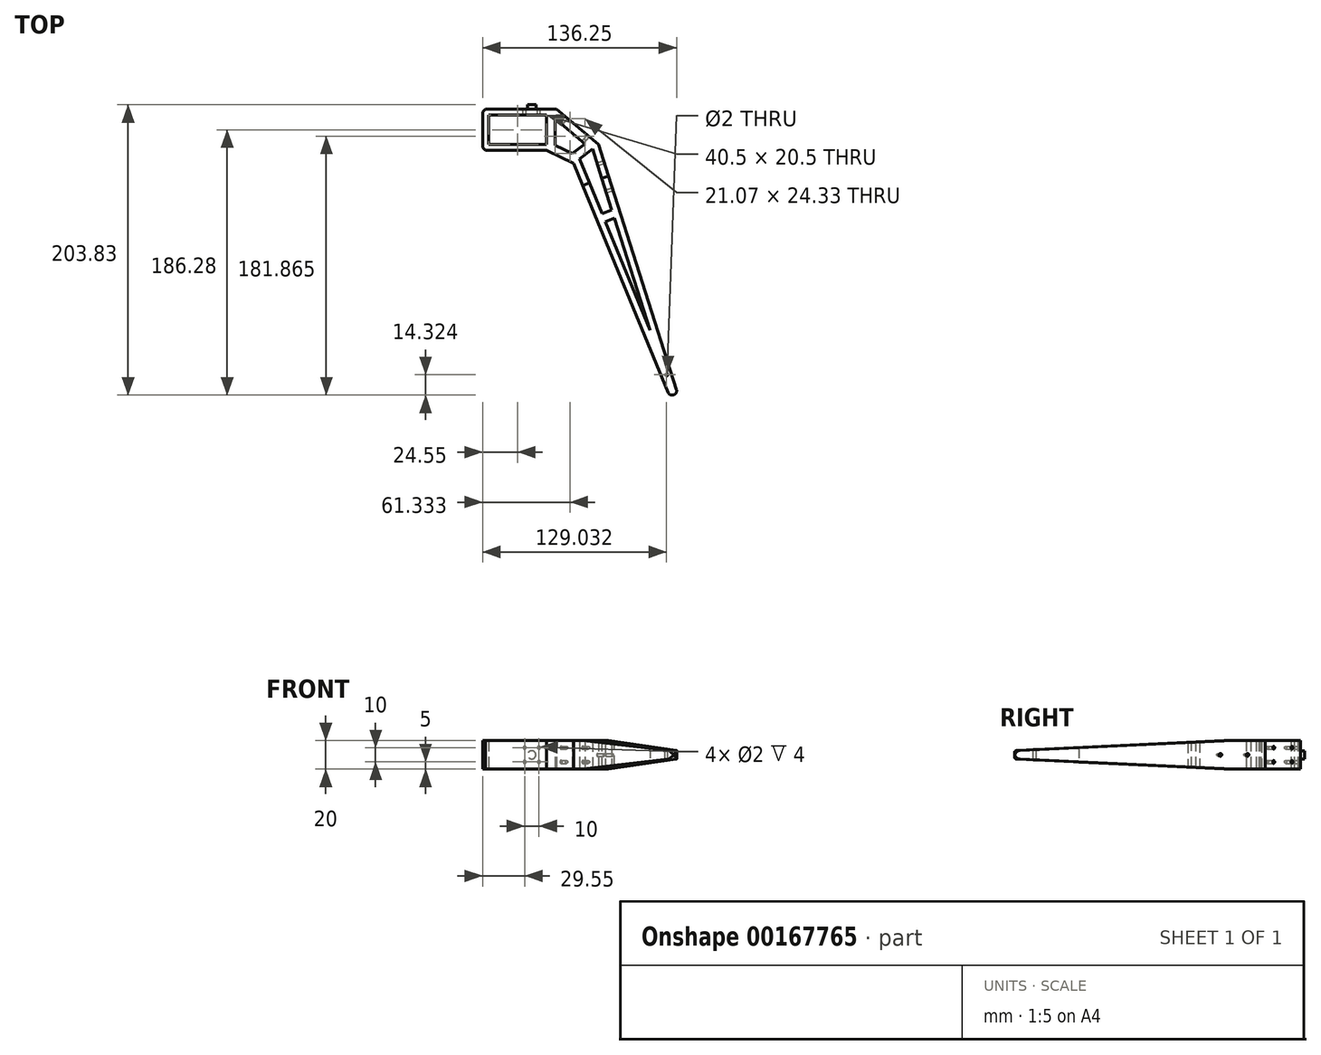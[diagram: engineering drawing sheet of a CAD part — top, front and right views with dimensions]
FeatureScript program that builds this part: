
annotation { "Feature Type Name" : "Feature", "Feature Type Description" : "" }
export const myFeature = defineFeature(function(context is Context, id is Id, definition is map)
    precondition{}
    {
        {
            var Q0;
            Q0=qCreatedBy(makeId("Top.planeOp"),FACE);
            var sketch = newSketch(context, id + "F0", { "sketchPlane" : qUnion([Q0])});
            skLineSegment(sketch, "E0.bottom", {"start": v(-40.5, 20.5) * mm, "end": v(0, 20.5) * mm});
            skLineSegment(sketch, "E0.top", {"start": v(-40.5, 0) * mm, "end": v(0, 0) * mm});
            skLineSegment(sketch, "E0.left", {"start": v(-40.5, 20.5) * mm, "end": v(-40.5, 0) * mm});
            skLineSegment(sketch, "E0.right", {"start": v(0, 20.5) * mm, "end": v(0, 0) * mm});
            skLineSegment(sketch, "E1", {"start": v(-44.8, 24.8) * mm, "end": v(-44.8, -4.3) * mm});
            skLineSegment(sketch, "E2", {"start": v(-44.8, -4.3) * mm, "end": v(0, -4.3) * mm});
            skLineSegment(sketch, "E3", {"start": v(0, -4.3) * mm, "end": v(19.04, -13.31) * mm});
            skLineSegment(sketch, "E4", {"start": v(36.56, 0) * mm, "end": v(7, 24.8) * mm});
            skLineSegment(sketch, "E5", {"start": v(7, 24.8) * mm, "end": v(-44.8, 24.8) * mm});
            skLineSegment(sketch, "E6", {"start": v(0, 20.5) * mm, "end": v(0, 24.8) * mm, "construction": true});
            skLineSegment(sketch, "E7", {"start": v(-40.5, 0) * mm, "end": v(-44.8, 0) * mm, "construction": true});
            skLineSegment(sketch, "E8", {"start": v(0, 0) * mm, "end": v(0, -4.3) * mm, "construction": true});
            skLineSegment(sketch, "E9", {"start": v(6, 18) * mm, "end": v(6, -0.5) * mm});
            skLineSegment(sketch, "E10", {"start": v(6, -0.5) * mm, "end": v(18.31, -6.33) * mm});
            skLineSegment(sketch, "E11", {"start": v(18.31, -6.33) * mm, "end": v(27.07, 0.32) * mm});
            skLineSegment(sketch, "E12", {"start": v(27.07, 0.32) * mm, "end": v(6, 18) * mm});
            skLineSegment(sketch, "E13", {"start": v(0, 10.25) * mm, "end": v(6, 10.25) * mm, "construction": true});
            skLineSegment(sketch, "E14", {"start": v(27.07, 0.32) * mm, "end": v(31.84, 3.95) * mm, "construction": true});
            skLineSegment(sketch, "E15", {"start": v(6, -0.5) * mm, "end": v(3.43, -5.93) * mm, "construction": true});
            skLineSegment(sketch, "E16", {"start": v(-40.5, 0) * mm, "end": v(0, 20.5) * mm, "construction": true});
            skLineSegment(sketch, "E17", {"start": v(-20.25, 10.25) * mm, "end": v(0, 0) * mm, "construction": true});
            skLineSegment(sketch, "E18", {"start": v(30.7, -4.45) * mm, "end": v(27.07, 0.32) * mm, "construction": true});
            skLineSegment(sketch, "E19", {"start": v(25.76, 60.45) * mm, "end": v(30.7, 61.23) * mm, "construction": true});
            skLineSegment(sketch, "E20", {"start": v(19.04, -13.31) * mm, "end": v(36.56, 0) * mm, "construction": true});
            skLineSegment(sketch, "E21", {"start": v(27.8, -6.66) * mm, "end": v(89.36, -175.8) * mm, "construction": true});
            skLineSegment(sketch, "E22", {"start": v(36.56, 0) * mm, "end": v(92.18, -174.78) * mm});
            skLineSegment(sketch, "E23", {"start": v(92.18, -174.78) * mm, "end": v(86.54, -176.83) * mm});
            skLineSegment(sketch, "E24", {"start": v(86.54, -176.83) * mm, "end": v(19.04, -13.31) * mm});
            skLineSegment(sketch, "E25", {"start": v(32.33, -3.21) * mm, "end": v(23.16, -10.18) * mm});
            skLineSegment(sketch, "E26", {"start": v(23.16, -10.18) * mm, "end": v(72.9, -130.66) * mm});
            skLineSegment(sketch, "E27", {"start": v(72.9, -130.66) * mm, "end": v(32.33, -3.21) * mm});
            skLineSegment(sketch, "E28", {"start": v(72.9, -130.66) * mm, "end": v(77.66, -129.14) * mm, "construction": true});
            skLineSegment(sketch, "E29", {"start": v(72.9, -130.66) * mm, "end": v(68.27, -132.57) * mm, "construction": true});
            skLineSegment(sketch, "E30", {"start": v(-30.5, 10.25) * mm, "end": v(89.36, -175.8) * mm, "construction": true});
            skLineSegment(sketch, "E31", {"start": v(-40.5, 10.25) * mm, "end": v(-30.5, 10.25) * mm, "construction": true});
            skSolve(sketch);
        }
        {
            var Q0;
            Q0=makeQuery(id+"F0.imprint","IMPRINT",FACE,{"disambiguationData":[TD([[makeQuery(id+"F0.imprint","IMPRINT",EDGE,{"derivedFrom":sQuery(id+"F0.wireOp",EDGE,"E0.bottom")}),1.0]])]});
            extrude(context, id + "F1", {"entities" : qUnion([Q0]), "endBound" : BoundingType.SYMMETRIC, "depth" : 20 * mm});
        }
        {
            var Q0;
            Q0=makeQuery(id+"F1.opExtrude","SWEPT_EDGE",EDGE,{"disambiguationData":[OSD([sQuery(id+"F0.wireOp",EDGE,"E1"),sQuery(id+"F0.wireOp",EDGE,"E5")])]});
            var Q1;
            Q1=makeQuery(id+"F1.opExtrude","SWEPT_EDGE",EDGE,{"disambiguationData":[OSD([sQuery(id+"F0.wireOp",EDGE,"E1"),sQuery(id+"F0.wireOp",EDGE,"E2")])]});
            chamfer(context, id + "F2", {"entities" : qUnion([Q0, Q1]), "width" : 2 * mm, "tangentPropagation" : true});
        }
        {
            var Q0;
            Q0=makeQuery(id+"F1.opExtrude","SWEPT_FACE",FACE,{"disambiguationData":[OSD([sQuery(id+"F0.wireOp",EDGE,"E5")])]});
            var sketch = newSketch(context, id + "F3", { "sketchPlane" : qUnion([Q0])});
            skLineSegment(sketch, "E32", {"start": v(10.25, 42.18) * mm, "end": v(10.25, -42.18) * mm, "construction": true});
            skCircle(sketch, "E33", {"center": v(10.25, 0) * mm, "radius": 2.9 * mm});
            skSolve(sketch);
        }
        {
            var Q0;
            Q0 = qSketchRegion(id + "F3", true);
            extrude(context, id + "F4", {"entities" : qUnion([Q0]), "operationType" : NewBodyOperationType.ADD, "depth" : 3 * mm});
        }
        {
            var Q0;
            Q0=makeQuery(id+"F1.opExtrude","CAP_VERTEX",VERTEX,{"disambiguationData":[OSD([sQuery(id+"F0.wireOp",EDGE,"E23"),sQuery(id+"F0.wireOp",EDGE,"E24")])],"isStart":true});
            var Q1;
            Q1=makeQuery(id+"F1.opExtrude","CAP_VERTEX",VERTEX,{"disambiguationData":[OSD([sQuery(id+"F0.wireOp",EDGE,"E22"),sQuery(id+"F0.wireOp",EDGE,"E23")])],"isStart":true});
            cPlane(context, id + "F5", {"entities" : qUnion([Q0, Q1]), "cplaneType" : CPlaneType.MID_PLANE, "offset" : 25 * mm, "width" : 150 * mm, "height" : 150 * mm});
        }
        {
            var Q0;
            Q0=qCreatedBy(id+"F5.planeOp",FACE);
            var sketch = newSketch(context, id + "F6", { "sketchPlane" : qUnion([Q0])});
            skLineSegment(sketch, "E34", {"start": v(-195.76, -3) * mm, "end": v(-35.76, -10) * mm});
            skLineSegment(sketch, "E35", {"start": v(-35.76, -10) * mm, "end": v(-195.76, -10) * mm});
            skLineSegment(sketch, "E36", {"start": v(-195.76, -10) * mm, "end": v(-195.76, -3) * mm});
            skLineSegment(sketch, "E37.MirrorCS", {"start": v(-195.76, 10) * mm, "end": v(-195.76, 3) * mm});
            skLineSegment(sketch, "E38.MirrorCS", {"start": v(-195.76, 3) * mm, "end": v(-35.76, 10) * mm});
            skLineSegment(sketch, "E39.MirrorCS", {"start": v(-35.76, 10) * mm, "end": v(-195.76, 10) * mm});
            skSolve(sketch);
        }
        {
            var Q0;
            Q0 = qSketchRegion(id + "F6", true);
            extrude(context, id + "F7", {"entities" : qUnion([Q0]), "operationType" : NewBodyOperationType.REMOVE, "endBound" : BoundingType.THROUGH_ALL, "oppositeDirection" : true, "depth" : 25 * mm, "hasSecondDirection" : true, "secondDirectionBound" : SecondDirectionBoundingType.THROUGH_ALL, "secondDirectionOppositeDirection" : false, "secondDirectionDepth" : 25 * mm});
        }
        {
            var Q0;
            Q0=makeQuery(id+"F1.opExtrude","SWEPT_EDGE",EDGE,{"disambiguationData":[OSD([sQuery(id+"F0.wireOp",EDGE,"E22"),sQuery(id+"F0.wireOp",EDGE,"E23")])]});
            var Q1;
            Q1=makeQuery(id+"F7.boolean.opBoolean","COPY",EDGE,{"derivedFrom":makeQuery(id+"F7.opExtrude","SWEPT_EDGE",EDGE,{"disambiguationData":[OSD([sQuery(id+"F6.wireOp",EDGE,"E37.MirrorCS"),sQuery(id+"F6.wireOp",EDGE,"E38.MirrorCS")])]})});
            var Q2;
            Q2=makeQuery(id+"F1.opExtrude","SWEPT_EDGE",EDGE,{"disambiguationData":[OSD([sQuery(id+"F0.wireOp",EDGE,"E23"),sQuery(id+"F0.wireOp",EDGE,"E24")])]});
            var Q3;
            Q3=makeQuery(id+"F7.boolean.opBoolean","COPY",EDGE,{"derivedFrom":makeQuery(id+"F7.opExtrude","SWEPT_EDGE",EDGE,{"disambiguationData":[OSD([sQuery(id+"F6.wireOp",EDGE,"E34"),sQuery(id+"F6.wireOp",EDGE,"E36")])]})});
            fillet(context, id + "F8", {"entities" : qUnion([Q0, Q1, Q2, Q3]), "radius" : 3 * mm, "tangentPropagation" : true});
        }
        {
            var Q0;
            Q0=makeQuery(id+"F1.opExtrude","SWEPT_FACE",FACE,{"disambiguationData":[OSD([sQuery(id+"F0.wireOp",EDGE,"E5")])]});
            var sketch = newSketch(context, id + "F9", { "sketchPlane" : qUnion([Q0])});
            skLineSegment(sketch, "E40.bottom", {"start": v(15.25, 5) * mm, "end": v(5.25, 5) * mm, "construction": true});
            skLineSegment(sketch, "E40.top", {"start": v(15.25, -5) * mm, "end": v(5.25, -5) * mm, "construction": true});
            skLineSegment(sketch, "E40.left", {"start": v(15.25, 5) * mm, "end": v(15.25, -5) * mm, "construction": true});
            skLineSegment(sketch, "E40.right", {"start": v(5.25, 5) * mm, "end": v(5.25, -5) * mm, "construction": true});
            skLineSegment(sketch, "E41", {"start": v(15.25, 5) * mm, "end": v(5.25, -5) * mm, "construction": true});
            skLineSegment(sketch, "E42", {"start": v(10.25, 0) * mm, "end": v(15.25, -5) * mm, "construction": true});
            skCircle(sketch, "E43", {"center": v(15.25, 5) * mm, "radius": 1 * mm});
            skCircle(sketch, "E44", {"center": v(15.25, -5) * mm, "radius": 1 * mm});
            skCircle(sketch, "E45", {"center": v(5.25, -5) * mm, "radius": 1 * mm});
            skCircle(sketch, "E46", {"center": v(5.25, 5) * mm, "radius": 1 * mm});
            skSolve(sketch);
        }
        {
            var Q0;
            Q0 = qSketchRegion(id + "F9", true);
            extrude(context, id + "F10", {"entities" : qUnion([Q0]), "operationType" : NewBodyOperationType.REMOVE, "oppositeDirection" : true, "depth" : 4 * mm, "offsetDistance" : 25 * mm});
        }
        {
            var Q0;
            Q0=qCreatedBy(id+"F5.planeOp",FACE);
            var sketch = newSketch(context, id + "F11", { "sketchPlane" : qUnion([Q0])});
            skLineSegment(sketch, "E47", {"start": v(-59.02, 8.98) * mm, "end": v(-65.02, 8.72) * mm});
            skLineSegment(sketch, "E48", {"start": v(-65.02, 8.72) * mm, "end": v(-65.02, -8.72) * mm});
            skLineSegment(sketch, "E49", {"start": v(-65.02, -8.72) * mm, "end": v(-59.02, -8.98) * mm});
            skLineSegment(sketch, "E50", {"start": v(-59.02, -8.98) * mm, "end": v(-59.02, 8.98) * mm});
            skSolve(sketch);
        }
        {
            var Q0;
            Q0 = qSketchRegion(id + "F11", true);
            extrude(context, id + "F12", {"entities" : qUnion([Q0]), "operationType" : NewBodyOperationType.ADD, "endBound" : BoundingType.UP_TO_NEXT, "depth" : 25 * mm, "offsetDistance" : 25 * mm, "hasSecondDirection" : true, "secondDirectionBound" : SecondDirectionBoundingType.UP_TO_NEXT, "secondDirectionOppositeDirection" : true, "secondDirectionDepth" : 25 * mm});
        }
        {
            var Q0;
            Q0=makeQuery(id+"F1.opExtrude","SWEPT_FACE",FACE,{"disambiguationData":[OSD([sQuery(id+"F0.wireOp",EDGE,"E4")])]});
            var sketch = newSketch(context, id + "F13", { "sketchPlane" : qUnion([Q0])});
            skLineSegment(sketch, "E51.bottom", {"start": v(1.29, 5) * mm, "end": v(-18.71, 5) * mm, "construction": true});
            skLineSegment(sketch, "E51.top", {"start": v(1.29, -5) * mm, "end": v(-18.71, -5) * mm, "construction": true});
            skLineSegment(sketch, "E51.left", {"start": v(1.29, 5) * mm, "end": v(1.29, -5) * mm, "construction": true});
            skLineSegment(sketch, "E51.right", {"start": v(-18.71, 5) * mm, "end": v(-18.71, -5) * mm, "construction": true});
            skCircle(sketch, "E52", {"center": v(1.29, 5) * mm, "radius": 1 * mm});
            skCircle(sketch, "E53", {"center": v(1.29, -5) * mm, "radius": 1 * mm});
            skCircle(sketch, "E54", {"center": v(-18.71, -5) * mm, "radius": 1 * mm});
            skCircle(sketch, "E55", {"center": v(-18.71, 5) * mm, "radius": 1 * mm});
            skLineSegment(sketch, "E56", {"start": v(-8.71, -10) * mm, "end": v(-8.71, 19.48) * mm, "construction": true});
            skSolve(sketch);
        }
        {
            var Q0;
            Q0 = qSketchRegion(id + "F13", true);
            extrude(context, id + "F14", {"entities" : qUnion([Q0]), "operationType" : NewBodyOperationType.REMOVE, "endBound" : BoundingType.UP_TO_NEXT, "oppositeDirection" : true, "depth" : 25 * mm, "offsetDistance" : 25 * mm});
        }
        {
            var Q0;
            Q0=makeQuery(id+"F1.opExtrude","SWEPT_FACE",FACE,{"disambiguationData":[OSD([sQuery(id+"F0.wireOp",EDGE,"E22")])]});
            var sketch = newSketch(context, id + "F15", { "sketchPlane" : qUnion([Q0])});
            skLineSegment(sketch, "E57", {"start": v(-24.09, 0) * mm, "end": v(-44.09, 0) * mm, "construction": true});
            skCircle(sketch, "E58", {"center": v(-24.09, 0) * mm, "radius": 1 * mm});
            skCircle(sketch, "E59", {"center": v(-44.09, 0) * mm, "radius": 1 * mm});
            skSolve(sketch);
        }
        {
            var Q0;
            Q0 = qSketchRegion(id + "F15", true);
            extrude(context, id + "F16", {"entities" : qUnion([Q0]), "operationType" : NewBodyOperationType.REMOVE, "endBound" : BoundingType.UP_TO_NEXT, "oppositeDirection" : true, "depth" : 25 * mm, "offsetDistance" : 25 * mm});
        }
        {
            var Q0;
            Q0=qCreatedBy(makeId("Top.planeOp"),FACE);
            var sketch = newSketch(context, id + "F17", { "sketchPlane" : qUnion([Q0])});
            skCircle(sketch, "E60", {"center": v(84.23, -161.7) * mm, "radius": 1 * mm});
            skSolve(sketch);
        }
        {
            var Q0;
            Q0 = qSketchRegion(id + "F17", true);
            extrude(context, id + "F18", {"entities" : qUnion([Q0]), "operationType" : NewBodyOperationType.REMOVE, "endBound" : BoundingType.THROUGH_ALL, "oppositeDirection" : true, "depth" : 25 * mm, "offsetDistance" : 25 * mm, "hasSecondDirection" : true, "secondDirectionBound" : SecondDirectionBoundingType.THROUGH_ALL, "secondDirectionOppositeDirection" : false, "secondDirectionDepth" : 25 * mm});
        }
    });
